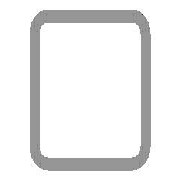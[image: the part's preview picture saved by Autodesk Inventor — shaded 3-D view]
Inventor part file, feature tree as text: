
AUTODESK INVENTOR PART (.ipt)
format: ipt  version: 2025 (Build 290162010, 162A)  size: 134,144 bytes
history: native  units: mm (DEFAULTED — no unit token found)
features: other x4, sketch x1, plane x1
ambient origin geometry x8: Origin, YZ Plane, XZ Plane, XY Plane, X Axis, Y Axis, Z Axis, Center Point
bodies: Solid1 (feature_tree), Body (feature_tree)
feature tree (6):
  parser-record x1  (decoder bookkeeping rows leaked as tree rows — omitted from the tree; the rows remain in map.json)
  other  "Driven Length"
  other  "Start Plane"
  other  "End Plane"
  sketch  "Sketch3"  dims[d3=1228.220213mm d4=0.0mm d7=6.0mm d9=80.0mm d11=80.0mm d12=3.0mm d13=80.0mm d14=1308.220213mm d15=40.0mm d16=40.0mm d17=90.0deg d18=1228.220213mm]
  plane  "Work Plane3"
